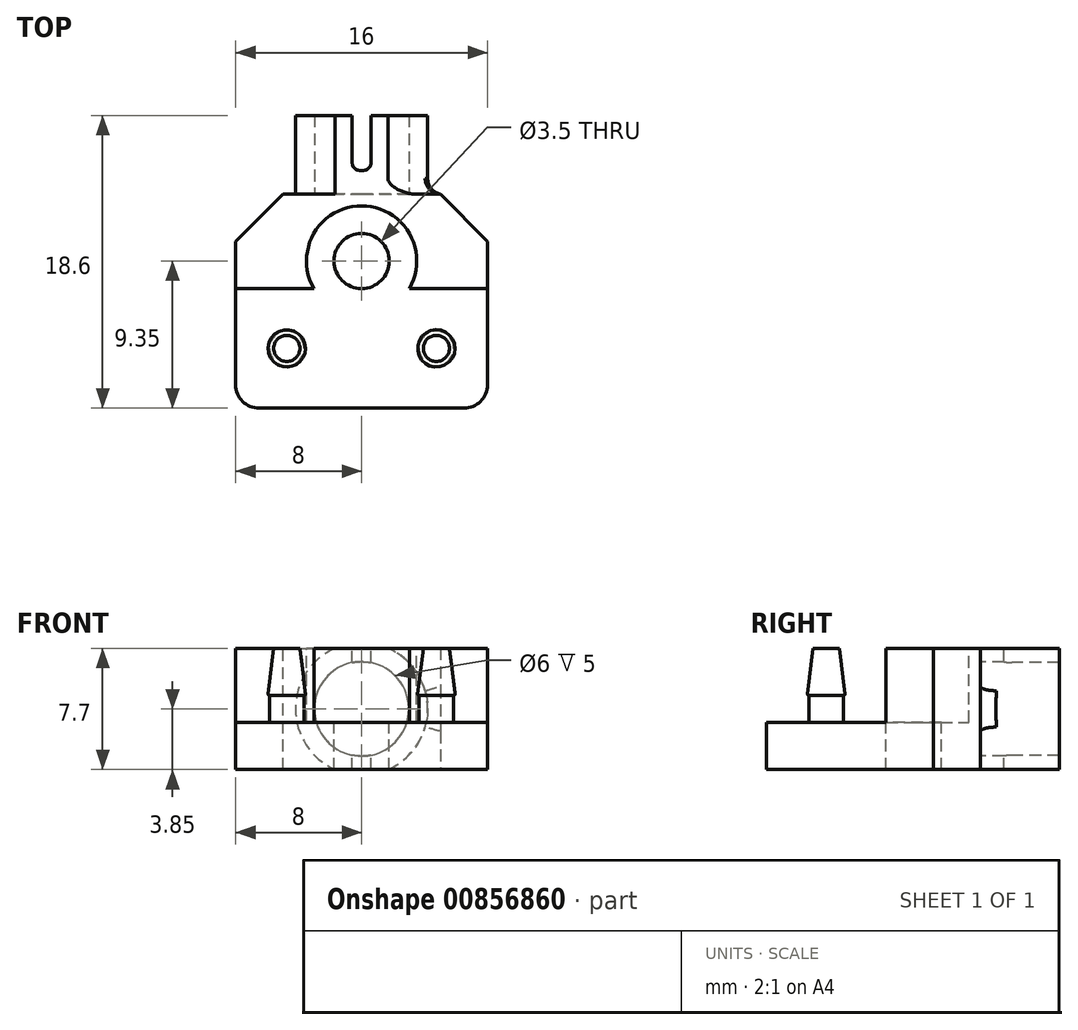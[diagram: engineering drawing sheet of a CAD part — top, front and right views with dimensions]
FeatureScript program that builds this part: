
annotation { "Feature Type Name" : "Feature", "Feature Type Description" : "" }
export const myFeature = defineFeature(function(context is Context, id is Id, definition is map)
    precondition{}
    {
        {
            var Q0;
            Q0=qCreatedBy(makeId("Top.planeOp"),FACE);
            var sketch = newSketch(context, id + "F0", { "sketchPlane" : qUnion([Q0])});
            skLineSegment(sketch, "E0.bottom", {"start": v(8, -3.8) * mm, "end": v(-8, -3.8) * mm});
            skLineSegment(sketch, "E0.top", {"start": v(8, 3.8) * mm, "end": v(-8, 3.8) * mm});
            skLineSegment(sketch, "E0.left", {"start": v(8, -3.8) * mm, "end": v(8, 3.8) * mm});
            skLineSegment(sketch, "E0.right", {"start": v(-8, -3.8) * mm, "end": v(-8, 3.8) * mm});
            skPoint(sketch, "E0.middle", {"position": v(0, 0) * mm});
            skSolve(sketch);
        }
        {
            var Q0;
            Q0=makeQuery(id+"F0.imprint","IMPRINT",FACE,{"disambiguationData":[TD([[makeQuery(id+"F0.imprint","IMPRINT",EDGE,{"derivedFrom":sQuery(id+"F0.wireOp",EDGE,"E0.bottom")}),-1.0]])]});
            extrude(context, id + "F1", {"entities" : qUnion([Q0]), "depth" : 3 * mm, "offsetDistance" : 25 * mm});
        }
        {
            var Q0;
            Q0=makeQuery(id+"F1.opExtrude","CAP_FACE",FACE,{"disambiguationData":[OSD([sQuery(id+"F0.wireOp",EDGE,"E0.bottom"),sQuery(id+"F0.wireOp",EDGE,"E0.top"),sQuery(id+"F0.wireOp",EDGE,"E0.left"),sQuery(id+"F0.wireOp",EDGE,"E0.right")])],"isStart":false});
            var sketch = newSketch(context, id + "F2", { "sketchPlane" : qUnion([Q0])});
            skCircle(sketch, "E1", {"center": v(-4.75, 0) * mm, "radius": 1.1 * mm});
            skCircle(sketch, "E2.MirrorC", {"center": v(4.75, 0) * mm, "radius": 1.1 * mm});
            skSolve(sketch);
        }
        {
            var Q0;
            Q0=qSketchRegion(id+"F2",true);
            extrude(context, id + "F3", {"entities" : qUnion([Q0]), "operationType" : NewBodyOperationType.ADD, "depth" : 1.7 * mm, "offsetDistance" : 25 * mm, "hasDraft" : true, "draftAngle" : 0 * degree, "draftPullDirection" : true});
        }
        {
            var Q0;
            Q0=qCreatedBy(makeId("Top.planeOp"),FACE);
            var sketch = newSketch(context, id + "F4", { "sketchPlane" : qUnion([Q0])});
            skLineSegment(sketch, "E3.bottom", {"start": v(-8, 3.8) * mm, "end": v(8, 3.8) * mm});
            skLineSegment(sketch, "E3.top", {"start": v(-8, 9.8) * mm, "end": v(8, 9.8) * mm});
            skLineSegment(sketch, "E3.left", {"start": v(-8, 3.8) * mm, "end": v(-8, 9.8) * mm});
            skLineSegment(sketch, "E3.right", {"start": v(8, 3.8) * mm, "end": v(8, 9.8) * mm});
            skSolve(sketch);
        }
        {
            var Q0;
            Q0=makeQuery(id+"F3.opExtrude","CAP_FACE",FACE,{"disambiguationData":[OSD([sQuery(id+"F2.wireOp",EDGE,"E1")])],"isStart":false});
            var sketch = newSketch(context, id + "F5", { "sketchPlane" : qUnion([Q0])});
            skCircle(sketch, "E4.0", {"center": v(-4.75, 0) * mm, "radius": 1.2 * mm});
            skCircle(sketch, "E5.MirrorC", {"center": v(4.75, 0) * mm, "radius": 1.2 * mm});
            skSolve(sketch);
        }
        {
            var Q0;
            Q0=qSketchRegion(id+"F5",true);
            extrude(context, id + "F6", {"entities" : qUnion([Q0]), "operationType" : NewBodyOperationType.ADD, "depth" : 3 * mm, "offsetDistance" : 25 * mm, "hasDraft" : true, "draftAngle" : 7 * degree, "draftPullDirection" : true});
        }
        {
            var Q0;
            Q0=makeQuery(id+"F6.opExtrude","CAP_EDGE",EDGE,{"disambiguationData":[OSD([sQuery(id+"F5.wireOp",EDGE,"E4.0")])],"isStart":true});
            var Q1;
            Q1=makeQuery(id+"F6.opExtrude","CAP_EDGE",EDGE,{"disambiguationData":[OSD([sQuery(id+"F5.wireOp",EDGE,"E5.MirrorC")])],"isStart":true});
            fillet(context, id + "F7", {"entities" : qUnion([Q0, Q1]), "radius" : 0.1 * mm, "tangentPropagation" : true, "allowEdgeOverflow" : false});
        }
        {
            var Q0;
            Q0=makeQuery(id+"F4.imprint","IMPRINT",FACE,{"disambiguationData":[TD([[makeQuery(id+"F4.imprint","IMPRINT",EDGE,{"derivedFrom":sQuery(id+"F4.wireOp",EDGE,"E3.bottom")}),1.0]])]});
            var Q1;
            Q1=makeQuery(id+"F6.opExtrude","CAP_FACE",FACE,{"disambiguationData":[OSD([sQuery(id+"F5.wireOp",EDGE,"E4.0")])],"isStart":false});
            extrude(context, id + "F8", {"entities" : qUnion([Q0]), "operationType" : NewBodyOperationType.ADD, "endBound" : BoundingType.UP_TO_SURFACE, "depth" : 6.5 * mm, "endBoundEntityFace" : qUnion([Q1]), "offsetDistance" : 25 * mm});
        }
        {
            var Q0;
            Q0=makeQuery(id+"F8.opExtrude","SWEPT_FACE",FACE,{"disambiguationData":[OSD([sQuery(id+"F4.wireOp",EDGE,"E3.top")])]});
            var sketch = newSketch(context, id + "F9", { "sketchPlane" : qUnion([Q0])});
            skCircle(sketch, "E6", {"center": v(0, 3.85) * mm, "radius": 3 * mm});
            skCircle(sketch, "E7.0", {"center": v(0, 3.85) * mm, "radius": 4.2 * mm});
            skSolve(sketch);
        }
        {
            var Q0;
            Q0=makeQuery(id+"F9.imprint","IMPRINT",FACE,{"disambiguationData":[TD([[makeQuery(id+"F9.imprint","IMPRINT",EDGE,{"derivedFrom":sQuery(id+"F9.wireOp",EDGE,"E6")}),-1.0]])]});
            extrude(context, id + "F10", {"entities" : qUnion([Q0]), "operationType" : NewBodyOperationType.ADD, "depth" : 5 * mm, "offsetDistance" : 25 * mm});
        }
        {
            var Q0;
            {var subQ0=sQuery(id+"F9.wireOp",EDGE,"E7.0");var subQ1=sQuery(id+"F4.wireOp",EDGE,"E3.top");var subQ2=makeQuery(id+"F8.opExtrude","CAP_EDGE",EDGE,{"disambiguationData":[OSD([subQ1])],"isStart":false});Q0=makeQuery(id+"F10.boolean.opBoolean","MERGE",FACE,{"derivedFrom":[makeQuery(id+"F8.opExtrude","CAP_FACE",FACE,{"disambiguationData":[OSD([sQuery(id+"F4.wireOp",EDGE,"E3.bottom"),subQ1,sQuery(id+"F4.wireOp",EDGE,"E3.left"),sQuery(id+"F4.wireOp",EDGE,"E3.right")])],"isStart":false}),makeQuery(id+"F10.opExtrude","SWEPT_FACE",FACE,{"disambiguationData":[OSD([subQ1]),TDD([makeQuery(id+"F9.imprint","IMPRINT",EDGE,{"disambiguationData":[TD([[makeQuery(id+"F9.imprint","INTERSECT",VERTEX,{"disambiguationData":[OD(0.0)],"derivedFrom":[subQ2,subQ0]}),1.0]])],"derivedFrom":subQ2})])]})]});}
            var sketch = newSketch(context, id + "F11", { "sketchPlane" : qUnion([Q0])});
            skLineSegment(sketch, "E8.bottom", {"start": v(0.6, 14.8) * mm, "end": v(-0.6, 14.8) * mm});
            skLineSegment(sketch, "E8.top", {"start": v(0.6, 11.3) * mm, "end": v(-0.6, 11.3) * mm});
            skLineSegment(sketch, "E8.left", {"start": v(0.6, 14.8) * mm, "end": v(0.6, 11.3) * mm});
            skLineSegment(sketch, "E8.right", {"start": v(-0.6, 14.8) * mm, "end": v(-0.6, 11.3) * mm});
            skPoint(sketch, "E8.middle", {"position": v(0, 13.05) * mm});
            skSolve(sketch);
        }
        {
            var Q0;
            Q0=makeQuery(id+"F11.imprint","IMPRINT",FACE,{"disambiguationData":[TD([[makeQuery(id+"F11.imprint","IMPRINT",EDGE,{"derivedFrom":sQuery(id+"F11.wireOp",EDGE,"E8.bottom")}),-1.0]])]});
            var Q1;
            {var subQ0=sQuery(id+"F9.wireOp",EDGE,"E7.0");var subQ1=sQuery(id+"F4.wireOp",EDGE,"E3.top");var subQ2=makeQuery(id+"F8.opExtrude","CAP_EDGE",EDGE,{"disambiguationData":[OSD([subQ1])],"isStart":true});Q1=makeQuery(id+"F10.boolean.opBoolean","MERGE",FACE,{"derivedFrom":[makeQuery(id+"F8.boolean.opBoolean","MERGE",FACE,{"derivedFrom":[makeQuery(id+"F1.opExtrude","CAP_FACE",FACE,{"disambiguationData":[OSD([sQuery(id+"F0.wireOp",EDGE,"E0.bottom"),sQuery(id+"F0.wireOp",EDGE,"E0.top"),sQuery(id+"F0.wireOp",EDGE,"E0.left"),sQuery(id+"F0.wireOp",EDGE,"E0.right")])],"isStart":true}),makeQuery(id+"F8.opExtrude","CAP_FACE",FACE,{"disambiguationData":[OSD([sQuery(id+"F4.wireOp",EDGE,"E3.bottom"),subQ1,sQuery(id+"F4.wireOp",EDGE,"E3.left"),sQuery(id+"F4.wireOp",EDGE,"E3.right")])],"isStart":true})]}),makeQuery(id+"F10.opExtrude","SWEPT_FACE",FACE,{"disambiguationData":[OSD([subQ1]),TDD([makeQuery(id+"F9.imprint","IMPRINT",EDGE,{"disambiguationData":[TD([[makeQuery(id+"F9.imprint","INTERSECT",VERTEX,{"disambiguationData":[OD(0.0)],"derivedFrom":[subQ2,subQ0]}),1.0]])],"derivedFrom":subQ2})])]})]});}
            extrude(context, id + "F12", {"entities" : qUnion([Q0]), "operationType" : NewBodyOperationType.REMOVE, "endBound" : BoundingType.UP_TO_SURFACE, "oppositeDirection" : true, "depth" : 25 * mm, "endBoundEntityFace" : qUnion([Q1]), "offsetDistance" : 25 * mm});
        }
        {
            var Q0;
            Q0=makeQuery(id+"F1.opExtrude","SWEPT_EDGE",EDGE,{"disambiguationData":[OSD([sQuery(id+"F0.wireOp",EDGE,"E0.bottom"),sQuery(id+"F0.wireOp",EDGE,"E0.right")])]});
            var Q1;
            Q1=makeQuery(id+"F1.opExtrude","SWEPT_EDGE",EDGE,{"disambiguationData":[OSD([sQuery(id+"F0.wireOp",EDGE,"E0.bottom"),sQuery(id+"F0.wireOp",EDGE,"E0.left")])]});
            fillet(context, id + "F13", {"entities" : qUnion([Q0, Q1]), "radius" : 1.5 * mm, "tangentPropagation" : true, "allowEdgeOverflow" : false});
        }
        {
            var Q0;
            {var subQ0=sQuery(id+"F9.wireOp",EDGE,"E7.0");var subQ1=sQuery(id+"F4.wireOp",EDGE,"E3.top");var subQ2=makeQuery(id+"F8.opExtrude","CAP_EDGE",EDGE,{"disambiguationData":[OSD([subQ1])],"isStart":false});var subQ3=sQuery(id+"F11.wireOp",EDGE,"E8.top");var subQ4=sQuery(id+"F11.wireOp",EDGE,"E8.right");Q0=makeQuery(id+"F12.boolean.opBoolean","COPY",EDGE,{"disambiguationData":[TD([makeQuery(id+"F10.opExtrude","SWEPT_FACE",FACE,{"disambiguationData":[OSD([subQ1]),TDD([makeQuery(id+"F9.imprint","IMPRINT",EDGE,{"disambiguationData":[TD([[makeQuery(id+"F9.imprint","INTERSECT",VERTEX,{"disambiguationData":[OD(0.0)],"derivedFrom":[subQ2,subQ0]}),1.0]])],"derivedFrom":subQ2})])]})])],"derivedFrom":makeQuery(id+"F12.opExtrude","SWEPT_EDGE",EDGE,{"disambiguationData":[OSD([subQ3,subQ4])]})});}
            var Q1;
            {var subQ0=sQuery(id+"F9.wireOp",EDGE,"E7.0");var subQ1=sQuery(id+"F4.wireOp",EDGE,"E3.top");var subQ2=makeQuery(id+"F8.opExtrude","CAP_EDGE",EDGE,{"disambiguationData":[OSD([subQ1])],"isStart":false});var subQ3=sQuery(id+"F11.wireOp",EDGE,"E8.top");var subQ4=sQuery(id+"F11.wireOp",EDGE,"E8.left");Q1=makeQuery(id+"F12.boolean.opBoolean","COPY",EDGE,{"disambiguationData":[TD([makeQuery(id+"F10.opExtrude","SWEPT_FACE",FACE,{"disambiguationData":[OSD([subQ1]),TDD([makeQuery(id+"F9.imprint","IMPRINT",EDGE,{"disambiguationData":[TD([[makeQuery(id+"F9.imprint","INTERSECT",VERTEX,{"disambiguationData":[OD(0.0)],"derivedFrom":[subQ2,subQ0]}),1.0]])],"derivedFrom":subQ2})])]})])],"derivedFrom":makeQuery(id+"F12.opExtrude","SWEPT_EDGE",EDGE,{"disambiguationData":[OSD([subQ3,subQ4])]})});}
            var Q2;
            {var subQ0=sQuery(id+"F9.wireOp",EDGE,"E7.0");var subQ1=sQuery(id+"F4.wireOp",EDGE,"E3.top");var subQ2=makeQuery(id+"F8.opExtrude","CAP_EDGE",EDGE,{"disambiguationData":[OSD([subQ1])],"isStart":true});var subQ3=sQuery(id+"F11.wireOp",EDGE,"E8.top");var subQ4=sQuery(id+"F11.wireOp",EDGE,"E8.left");Q2=makeQuery(id+"F12.boolean.opBoolean","COPY",EDGE,{"disambiguationData":[TD([makeQuery(id+"F10.opExtrude","SWEPT_FACE",FACE,{"disambiguationData":[OSD([subQ1]),TDD([makeQuery(id+"F9.imprint","IMPRINT",EDGE,{"disambiguationData":[TD([[makeQuery(id+"F9.imprint","INTERSECT",VERTEX,{"disambiguationData":[OD(0.0)],"derivedFrom":[subQ2,subQ0]}),1.0]])],"derivedFrom":subQ2})])]})])],"derivedFrom":makeQuery(id+"F12.opExtrude","SWEPT_EDGE",EDGE,{"disambiguationData":[OSD([subQ3,subQ4])]})});}
            var Q3;
            {var subQ0=sQuery(id+"F9.wireOp",EDGE,"E7.0");var subQ1=sQuery(id+"F4.wireOp",EDGE,"E3.top");var subQ2=makeQuery(id+"F8.opExtrude","CAP_EDGE",EDGE,{"disambiguationData":[OSD([subQ1])],"isStart":true});var subQ3=sQuery(id+"F11.wireOp",EDGE,"E8.top");var subQ4=sQuery(id+"F11.wireOp",EDGE,"E8.right");Q3=makeQuery(id+"F12.boolean.opBoolean","COPY",EDGE,{"disambiguationData":[TD([makeQuery(id+"F10.opExtrude","SWEPT_FACE",FACE,{"disambiguationData":[OSD([subQ1]),TDD([makeQuery(id+"F9.imprint","IMPRINT",EDGE,{"disambiguationData":[TD([[makeQuery(id+"F9.imprint","INTERSECT",VERTEX,{"disambiguationData":[OD(0.0)],"derivedFrom":[subQ2,subQ0]}),1.0]])],"derivedFrom":subQ2})])]})])],"derivedFrom":makeQuery(id+"F12.opExtrude","SWEPT_EDGE",EDGE,{"disambiguationData":[OSD([subQ3,subQ4])]})});}
            fillet(context, id + "F14", {"entities" : qUnion([Q0, Q1, Q2, Q3]), "radius" : 0.5 * mm, "tangentPropagation" : true, "allowEdgeOverflow" : false});
        }
        {
            var Q0;
            {var subQ0=sQuery(id+"F9.wireOp",EDGE,"E7.0");var subQ1=sQuery(id+"F4.wireOp",EDGE,"E3.top");var subQ2=makeQuery(id+"F8.opExtrude","CAP_EDGE",EDGE,{"disambiguationData":[OSD([subQ1])],"isStart":false});Q0=makeQuery(id+"F10.boolean.opBoolean","MERGE",FACE,{"derivedFrom":[makeQuery(id+"F8.opExtrude","CAP_FACE",FACE,{"disambiguationData":[OSD([sQuery(id+"F4.wireOp",EDGE,"E3.bottom"),subQ1,sQuery(id+"F4.wireOp",EDGE,"E3.left"),sQuery(id+"F4.wireOp",EDGE,"E3.right")])],"isStart":false}),makeQuery(id+"F10.opExtrude","SWEPT_FACE",FACE,{"disambiguationData":[OSD([subQ1]),TDD([makeQuery(id+"F9.imprint","IMPRINT",EDGE,{"disambiguationData":[TD([[makeQuery(id+"F9.imprint","INTERSECT",VERTEX,{"disambiguationData":[OD(0.0)],"derivedFrom":[subQ2,subQ0]}),1.0]])],"derivedFrom":subQ2})])]})]});}
            var sketch = newSketch(context, id + "F15", { "sketchPlane" : qUnion([Q0])});
            skCircle(sketch, "E9", {"center": v(0, 5.55) * mm, "radius": 3.5 * mm});
            skPoint(sketch, "E10", {"position": v(0, 3.8) * mm});
            skCircle(sketch, "E11", {"center": v(0, 5.55) * mm, "radius": 1.75 * mm});
            skSolve(sketch);
        }
        {
            var Q0;
            {var subQ4=sQuery(id+"F15.wireOp",EDGE,"E11");Q0=makeQuery(id+"F15.imprint","IMPRINT",FACE,{"disambiguationData":[TD([[makeQuery(id+"F15.imprint","IMPRINT",EDGE,{"derivedFrom":subQ4}),-1.0]])]});}
            var Q1;
            Q1=makeQuery(id+"F15.imprint","IMPRINT",FACE,{"disambiguationData":[TD([[makeQuery(id+"F15.imprint","IMPRINT",EDGE,{"derivedFrom":sQuery(id+"F15.wireOp",EDGE,"E11")}),1.0]])]});
            var Q2;
            Q2=makeQuery(id+"F1.opExtrude","CAP_FACE",FACE,{"disambiguationData":[OSD([sQuery(id+"F0.wireOp",EDGE,"E0.bottom"),sQuery(id+"F0.wireOp",EDGE,"E0.top"),sQuery(id+"F0.wireOp",EDGE,"E0.left"),sQuery(id+"F0.wireOp",EDGE,"E0.right")])],"isStart":false});
            extrude(context, id + "F16", {"entities" : qUnion([Q0, Q1]), "operationType" : NewBodyOperationType.REMOVE, "endBound" : BoundingType.UP_TO_SURFACE, "oppositeDirection" : true, "depth" : 4.6 * mm, "endBoundEntityFace" : qUnion([Q2]), "offsetDistance" : 25 * mm});
        }
        {
            var Q0;
            Q0=makeQuery(id+"F15.imprint","IMPRINT",FACE,{"disambiguationData":[TD([[makeQuery(id+"F15.imprint","IMPRINT",EDGE,{"derivedFrom":sQuery(id+"F15.wireOp",EDGE,"E11")}),1.0]])]});
            var Q1;
            {var subQ0=sQuery(id+"F9.wireOp",EDGE,"E7.0");var subQ1=sQuery(id+"F4.wireOp",EDGE,"E3.top");var subQ2=makeQuery(id+"F8.opExtrude","CAP_EDGE",EDGE,{"disambiguationData":[OSD([subQ1])],"isStart":true});Q1=makeQuery(id+"F10.boolean.opBoolean","MERGE",FACE,{"derivedFrom":[makeQuery(id+"F8.boolean.opBoolean","MERGE",FACE,{"derivedFrom":[makeQuery(id+"F1.opExtrude","CAP_FACE",FACE,{"disambiguationData":[OSD([sQuery(id+"F0.wireOp",EDGE,"E0.bottom"),sQuery(id+"F0.wireOp",EDGE,"E0.top"),sQuery(id+"F0.wireOp",EDGE,"E0.left"),sQuery(id+"F0.wireOp",EDGE,"E0.right")])],"isStart":true}),makeQuery(id+"F8.opExtrude","CAP_FACE",FACE,{"disambiguationData":[OSD([sQuery(id+"F4.wireOp",EDGE,"E3.bottom"),subQ1,sQuery(id+"F4.wireOp",EDGE,"E3.left"),sQuery(id+"F4.wireOp",EDGE,"E3.right")])],"isStart":true})]}),makeQuery(id+"F10.opExtrude","SWEPT_FACE",FACE,{"disambiguationData":[OSD([subQ1]),TDD([makeQuery(id+"F9.imprint","IMPRINT",EDGE,{"disambiguationData":[TD([[makeQuery(id+"F9.imprint","INTERSECT",VERTEX,{"disambiguationData":[OD(0.0)],"derivedFrom":[subQ2,subQ0]}),1.0]])],"derivedFrom":subQ2})])]})]});}
            extrude(context, id + "F17", {"entities" : qUnion([Q0]), "operationType" : NewBodyOperationType.REMOVE, "endBound" : BoundingType.UP_TO_SURFACE, "oppositeDirection" : true, "depth" : 25 * mm, "endBoundEntityFace" : qUnion([Q1]), "offsetDistance" : 25 * mm});
        }
        {
            var Q0;
            Q0=makeQuery(id+"F8.opExtrude","SWEPT_EDGE",EDGE,{"disambiguationData":[OSD([sQuery(id+"F4.wireOp",EDGE,"E3.top"),sQuery(id+"F4.wireOp",EDGE,"E3.left")])]});
            var Q1;
            Q1=makeQuery(id+"F8.opExtrude","SWEPT_EDGE",EDGE,{"disambiguationData":[OSD([sQuery(id+"F4.wireOp",EDGE,"E3.top"),sQuery(id+"F4.wireOp",EDGE,"E3.right")])]});
            chamfer(context, id + "F18", {"entities" : qUnion([Q0, Q1]), "width" : 3 * mm, "tangentPropagation" : true});
        }
        {
            var Q0;
            {var subQ0=sQuery(id+"F9.wireOp",EDGE,"E7.0");var subQ1=sQuery(id+"F4.wireOp",EDGE,"E3.top");Q0=makeQuery(id+"F10.opExtrude","CAP_EDGE",EDGE,{"disambiguationData":[OSD([subQ0]),TDD([makeQuery(id+"F9.imprint","IMPRINT",EDGE,{"disambiguationData":[TD([[makeQuery(id+"F9.imprint","INTERSECT",VERTEX,{"disambiguationData":[OD(0.0)],"derivedFrom":[makeQuery(id+"F8.opExtrude","CAP_EDGE",EDGE,{"disambiguationData":[OSD([subQ1])],"isStart":false}),subQ0]}),-1.0]])],"derivedFrom":subQ0})])],"isStart":true});}
            var Q1;
            {var subQ0=sQuery(id+"F9.wireOp",EDGE,"E7.0");var subQ1=sQuery(id+"F4.wireOp",EDGE,"E3.top");Q1=makeQuery(id+"F10.opExtrude","CAP_EDGE",EDGE,{"disambiguationData":[OSD([subQ0]),TDD([makeQuery(id+"F9.imprint","IMPRINT",EDGE,{"disambiguationData":[TD([[makeQuery(id+"F9.imprint","INTERSECT",VERTEX,{"disambiguationData":[OD(1.0)],"derivedFrom":[makeQuery(id+"F8.opExtrude","CAP_EDGE",EDGE,{"disambiguationData":[OSD([subQ1])],"isStart":false}),subQ0]}),1.0]])],"derivedFrom":subQ0})])],"isStart":true});}
            fillet(context, id + "F19", {"entities" : qUnion([Q0, Q1]), "radius" : 1 * mm, "tangentPropagation" : true, "allowEdgeOverflow" : false});
        }
    });
